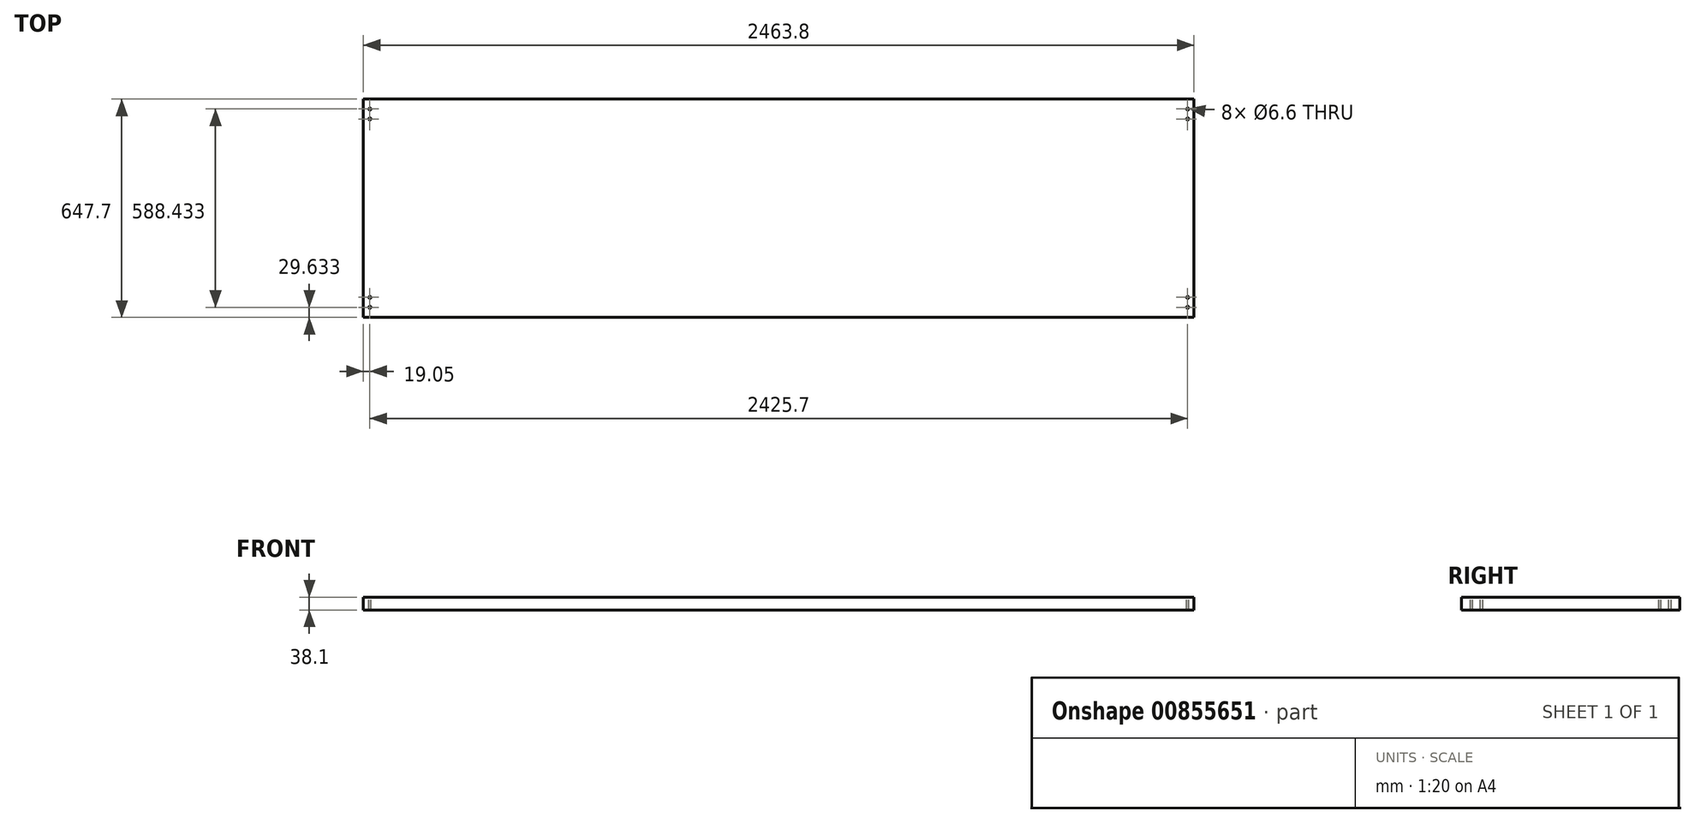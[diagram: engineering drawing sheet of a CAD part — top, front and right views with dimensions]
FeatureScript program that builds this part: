
annotation { "Feature Type Name" : "Feature", "Feature Type Description" : "" }
export const myFeature = defineFeature(function(context is Context, id is Id, definition is map)
    precondition{}
    {
        {
            var Q0;
            Q0=qCreatedBy(makeId("Top.planeOp"),FACE);
            var sketch = newSketch(context, id + "F0", { "sketchPlane" : qUnion([Q0])});
            skLineSegment(sketch, "E0.bottom", {"start": v(1231.9, 323.85) * mm, "end": v(-1231.9, 323.85) * mm});
            skLineSegment(sketch, "E0.top", {"start": v(1231.9, -323.85) * mm, "end": v(-1231.9, -323.85) * mm});
            skLineSegment(sketch, "E0.left", {"start": v(1231.9, 323.85) * mm, "end": v(1231.9, -323.85) * mm});
            skLineSegment(sketch, "E0.right", {"start": v(-1231.9, 323.85) * mm, "end": v(-1231.9, -323.85) * mm});
            skPoint(sketch, "E0.middle", {"position": v(0, 0) * mm});
            skSolve(sketch);
        }
        {
            var Q0;
            Q0=makeQuery(id+"F0.imprint","IMPRINT",FACE,{"disambiguationData":[TD([[makeQuery(id+"F0.imprint","IMPRINT",EDGE,{"derivedFrom":sQuery(id+"F0.wireOp",EDGE,"E0.bottom")}),1.0]])]});
            extrude(context, id + "F1", {"entities" : qUnion([Q0]), "depth" : 38.1 * mm, "offsetDistance" : 25.4 * mm});
        }
        {
            var Q0;
            Q0=makeQuery(id+"F1.opExtrude","CAP_FACE",FACE,{"disambiguationData":[OSD([sQuery(id+"F0.wireOp",EDGE,"E0.bottom"),sQuery(id+"F0.wireOp",EDGE,"E0.top"),sQuery(id+"F0.wireOp",EDGE,"E0.left"),sQuery(id+"F0.wireOp",EDGE,"E0.right")])],"isStart":false});
            var sketch = newSketch(context, id + "F2", { "sketchPlane" : qUnion([Q0])});
            skLineSegment(sketch, "E1", {"start": v(-1231.9, 234.95) * mm, "end": v(1231.9, 234.95) * mm, "construction": true});
            skLineSegment(sketch, "E2", {"start": v(1231.9, -234.95) * mm, "end": v(-1231.9, -234.95) * mm, "construction": true});
            skLineSegment(sketch, "E3", {"start": v(-1193.8, 323.85) * mm, "end": v(-1193.8, -323.85) * mm, "construction": true});
            skLineSegment(sketch, "E4", {"start": v(1193.8, 323.85) * mm, "end": v(1193.8, -323.85) * mm, "construction": true});
            skLineSegment(sketch, "E5", {"start": v(-1212.85, 323.85) * mm, "end": v(-1212.85, -323.85) * mm, "construction": true});
            skLineSegment(sketch, "E6", {"start": v(1212.85, 323.85) * mm, "end": v(1212.85, -323.85) * mm, "construction": true});
            skLineSegment(sketch, "E7", {"start": v(-1231.9, 294.22) * mm, "end": v(1231.9, 294.22) * mm, "construction": true});
            skLineSegment(sketch, "E8", {"start": v(-1231.9, 264.58) * mm, "end": v(1231.9, 264.58) * mm, "construction": true});
            skCircle(sketch, "E9", {"center": v(-1212.85, 294.22) * mm, "radius": 3.3 * mm});
            skCircle(sketch, "E10", {"center": v(-1212.85, 264.58) * mm, "radius": 3.3 * mm});
            skCircle(sketch, "E11", {"center": v(1212.85, 294.22) * mm, "radius": 3.3 * mm});
            skCircle(sketch, "E12", {"center": v(1212.85, 264.58) * mm, "radius": 3.3 * mm});
            skLineSegment(sketch, "E13", {"start": v(-1231.9, -264.58) * mm, "end": v(1231.9, -264.58) * mm, "construction": true});
            skLineSegment(sketch, "E14", {"start": v(1231.9, -294.22) * mm, "end": v(-1231.9, -294.22) * mm, "construction": true});
            skCircle(sketch, "E15", {"center": v(-1212.85, -264.58) * mm, "radius": 3.3 * mm});
            skCircle(sketch, "E16", {"center": v(-1212.85, -294.22) * mm, "radius": 3.3 * mm});
            skCircle(sketch, "E17", {"center": v(1212.85, -264.58) * mm, "radius": 3.3 * mm});
            skCircle(sketch, "E18", {"center": v(1212.85, -294.22) * mm, "radius": 3.3 * mm});
            skSolve(sketch);
        }
        {
            var Q0;
            Q0 = qSketchRegion(id + "F2", true);
            extrude(context, id + "F3", {"entities" : qUnion([Q0]), "operationType" : NewBodyOperationType.REMOVE, "endBound" : BoundingType.THROUGH_ALL, "oppositeDirection" : true, "depth" : 25.4 * mm, "offsetDistance" : 25.4 * mm});
        }
    });
